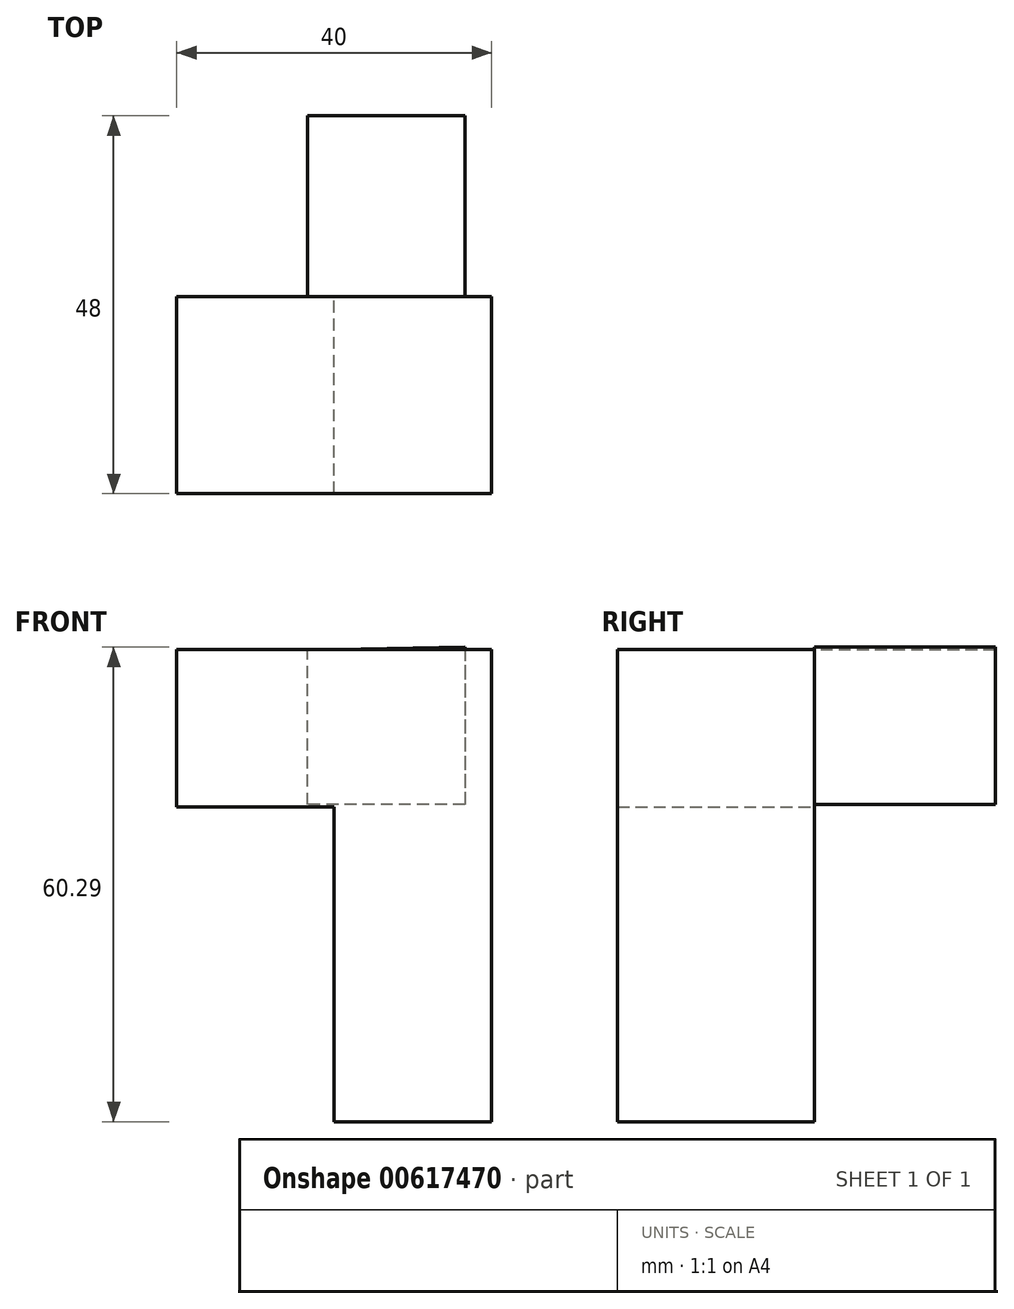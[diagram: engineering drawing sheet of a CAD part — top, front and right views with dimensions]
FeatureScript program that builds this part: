
annotation { "Feature Type Name" : "Feature", "Feature Type Description" : "" }
export const myFeature = defineFeature(function(context is Context, id is Id, definition is map)
    precondition{}
    {
        {
            var Q0;
            Q0=qCreatedBy(makeId("Front.planeOp"),FACE);
            var sketch = newSketch(context, id + "F0", { "sketchPlane" : qUnion([Q0])});
            skLineSegment(sketch, "E0", {"start": v(-7.02, 29.93) * mm, "end": v(-7.02, 9.93) * mm});
            skLineSegment(sketch, "E1", {"start": v(-7.02, 9.93) * mm, "end": v(-27.02, 9.93) * mm});
            skLineSegment(sketch, "E2", {"start": v(-27.02, 9.58) * mm, "end": v(-27.02, 29.58) * mm});
            skLineSegment(sketch, "E3", {"start": v(-27.02, 29.58) * mm, "end": v(-7.02, 29.93) * mm});
            skSolve(sketch);
        }
        {
            var Q0;
            Q0 = qSketchRegion(id + "F0", true);
            var Q1;
            {var subQ0=sQuery(id+"F0.wireOp",EDGE,"E0");Q1=makeQuery(id+"F0.imprint","IMPRINT",FACE,{"disambiguationData":[TD([[makeQuery(id+"F0.imprint","IMPRINT",EDGE,{"derivedFrom":subQ0}),-1.0]])]});}
            extrude(context, id + "F1", {"entities" : qUnion([Q0, Q1]), "oppositeDirection" : true, "depth" : 23 * mm, "offsetDistance" : 25 * mm});
        }
        {
            var Q0;
            Q0=qCreatedBy(makeId("Front.planeOp"),FACE);
            var sketch = newSketch(context, id + "F2", { "sketchPlane" : qUnion([Q0])});
            skLineSegment(sketch, "E4", {"start": v(-3.64, 29.64) * mm, "end": v(-43.64, 29.64) * mm});
            skLineSegment(sketch, "E5", {"start": v(-43.64, 29.64) * mm, "end": v(-43.64, 9.64) * mm});
            skLineSegment(sketch, "E6", {"start": v(-43.64, 9.64) * mm, "end": v(-23.64, 9.64) * mm});
            skLineSegment(sketch, "E7", {"start": v(-23.64, 9.64) * mm, "end": v(-23.64, -30.36) * mm});
            skLineSegment(sketch, "E8", {"start": v(-23.64, -30.36) * mm, "end": v(-3.64, -30.36) * mm});
            skLineSegment(sketch, "E9", {"start": v(-3.64, -30.36) * mm, "end": v(-3.64, 29.64) * mm});
            skLineSegment(sketch, "E10", {"start": v(-3.64, 29.64) * mm, "end": v(-3.64, 29.64) * mm});
            skSolve(sketch);
        }
        {
            var Q0;
            Q0 = qSketchRegion(id + "F2", true);
            extrude(context, id + "F3", {"entities" : qUnion([Q0]), "operationType" : NewBodyOperationType.ADD, "depth" : 25 * mm, "offsetDistance" : 25 * mm});
        }
    });
